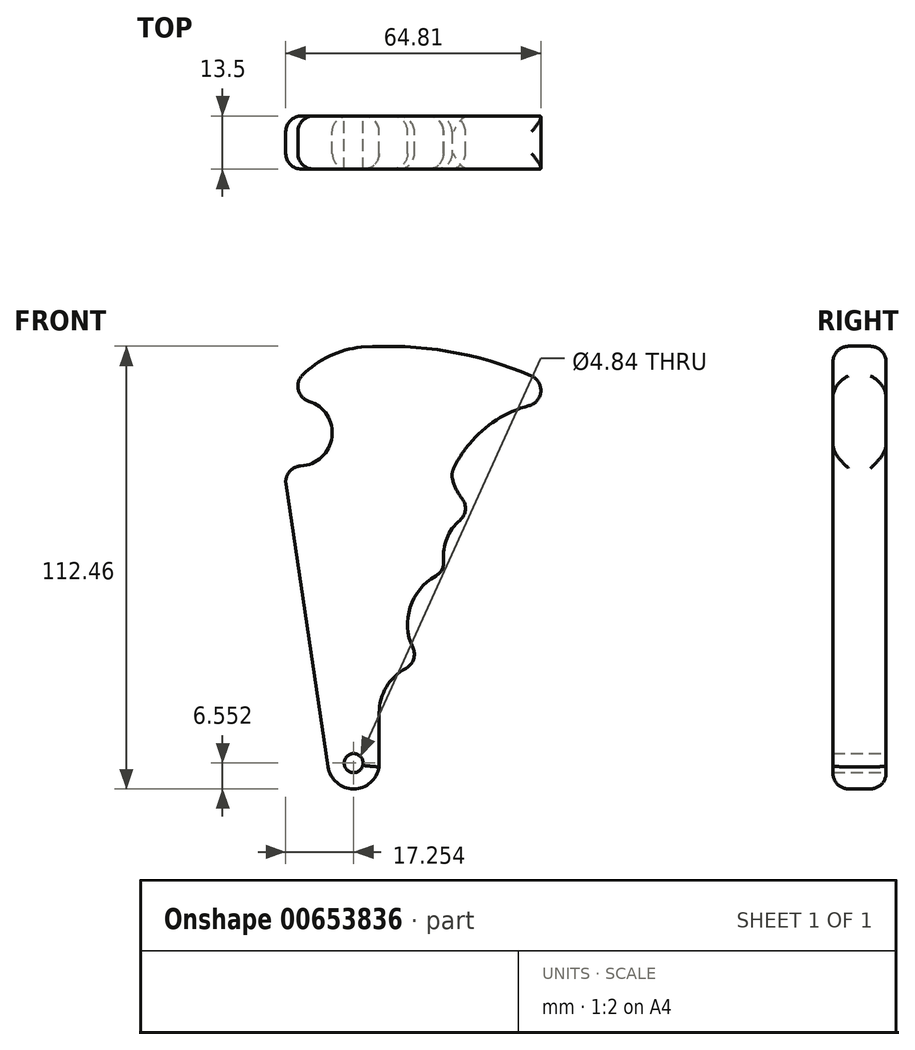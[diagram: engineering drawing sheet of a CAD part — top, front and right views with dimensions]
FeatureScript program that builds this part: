
annotation { "Feature Type Name" : "Feature", "Feature Type Description" : "" }
export const myFeature = defineFeature(function(context is Context, id is Id, definition is map)
    precondition{}
    {
        {
            var Q0;
            Q0=qCreatedBy(makeId("Front.planeOp"),FACE);
            var sketch = newSketch(context, id + "F0", { "sketchPlane" : qUnion([Q0])});
            skLineSegment(sketch, "E0", {"start": v(-37.75, -42.23) * mm, "end": v(-49.34, 35.35) * mm});
            skArc(sketch, "E1", {"start": v(-37.75, -42.23) * mm, "mid": v(-31.28, -47.82) * mm, "end": v(-24.8, -42.23) * mm});
            skCircle(sketch, "E2", {"center": v(-31.28, -41.27) * mm, "radius": 2.42 * mm});
            skPoint(sketch, "E3", {"position": v(-31.28, -47.82) * mm});
            skLineSegment(sketch, "E4", {"start": v(-69.41, 40.12) * mm, "end": v(-69.41, 40.12) * mm});
            skPoint(sketch, "E5", {"position": v(-29.29, 64.41) * mm});
            skLineSegment(sketch, "E6", {"start": v(-24.8, -42.23) * mm, "end": v(-24.8, -28.55) * mm});
            skArc(sketch, "E7", {"start": v(-13.59, -15.8) * mm, "mid": v(-21.6, -20.06) * mm, "end": v(-24.8, -28.55) * mm});
            skArc(sketch, "E8", {"start": v(-7.8, 7.43) * mm, "mid": v(-17.15, -2.58) * mm, "end": v(-13.59, -15.8) * mm});
            skArc(sketch, "E9", {"start": v(0, 22.78) * mm, "mid": v(-7.17, 16.77) * mm, "end": v(-7.8, 7.43) * mm});
            skPoint(sketch, "E10", {"position": v(-24.8, -28.55) * mm});
            skPoint(sketch, "E11", {"position": v(-39.8, -28.55) * mm});
            skPoint(sketch, "E12", {"position": v(-15.77, -12.87) * mm});
            skPoint(sketch, "E13", {"position": v(-38.58, -36.72) * mm});
            skPoint(sketch, "E14", {"position": v(-7.17, 16.77) * mm});
            skPoint(sketch, "E15", {"position": v(-44.06, 0) * mm});
            skPoint(sketch, "E16", {"position": v(-6.44, 32.37) * mm});
            skPoint(sketch, "E17", {"position": v(-49.34, 35.35) * mm});
            skPoint(sketch, "E18", {"position": v(-47.46, 22.78) * mm});
            skArc(sketch, "E19", {"start": v(-49.34, 35.35) * mm, "mid": v(-36.7, 42.63) * mm, "end": v(-49.34, 49.9) * mm});
            skArc(sketch, "E20", {"start": v(-29.29, 64.41) * mm, "mid": v(-41.27, 59.87) * mm, "end": v(-49.34, 49.9) * mm});
            skArc(sketch, "E21", {"start": v(27.44, 49.9) * mm, "mid": v(0.24, 61.74) * mm, "end": v(-29.29, 64.41) * mm});
            skArc(sketch, "E22", {"start": v(27.44, 49.9) * mm, "mid": v(7.33, 47.25) * mm, "end": v(-6.44, 32.37) * mm});
            skArc(sketch, "E23", {"start": v(-6.44, 32.37) * mm, "mid": v(-4.36, 26.8) * mm, "end": v(0, 22.78) * mm});
            skSolve(sketch);
        }
        {
            var Q0;
            Q0 = qSketchRegion(id + "F0", true);
            extrude(context, id + "F1", {"entities" : qUnion([Q0]), "depth" : 13.5 * mm, "offsetDistance" : 25 * mm});
        }
        {
            var Q0;
            Q0=makeQuery(id+"F1.opExtrude","SWEPT_FACE",FACE,{"disambiguationData":[OSD([sQuery(id+"F0.wireOp",EDGE,"E23")])]});
            var Q1;
            Q1=makeQuery(id+"F1.opExtrude","SWEPT_FACE",FACE,{"disambiguationData":[OSD([sQuery(id+"F0.wireOp",EDGE,"E9")])]});
            var Q2;
            Q2=makeQuery(id+"F1.opExtrude","SWEPT_FACE",FACE,{"disambiguationData":[OSD([sQuery(id+"F0.wireOp",EDGE,"E8")])]});
            var Q3;
            Q3=makeQuery(id+"F1.opExtrude","SWEPT_FACE",FACE,{"disambiguationData":[OSD([sQuery(id+"F0.wireOp",EDGE,"E7")])]});
            var Q4;
            Q4=makeQuery(id+"F1.opExtrude","SWEPT_FACE",FACE,{"disambiguationData":[OSD([sQuery(id+"F0.wireOp",EDGE,"E0")])]});
            var Q5;
            Q5=makeQuery(id+"F1.opExtrude","SWEPT_FACE",FACE,{"disambiguationData":[OSD([sQuery(id+"F0.wireOp",EDGE,"E21")])]});
            var Q6;
            Q6=makeQuery(id+"F1.opExtrude","SWEPT_FACE",FACE,{"disambiguationData":[OSD([sQuery(id+"F0.wireOp",EDGE,"E20")])]});
            var Q7;
            Q7=makeQuery(id+"F1.opExtrude","SWEPT_FACE",FACE,{"disambiguationData":[OSD([sQuery(id+"F0.wireOp",EDGE,"E19")])]});
            fillet(context, id + "F2", {"entities" : qUnion([Q0, Q1, Q2, Q3, Q4, Q5, Q6, Q7]), "radius" : 4 * mm, "tangentPropagation" : true, "allowEdgeOverflow" : false});
        }
    });
